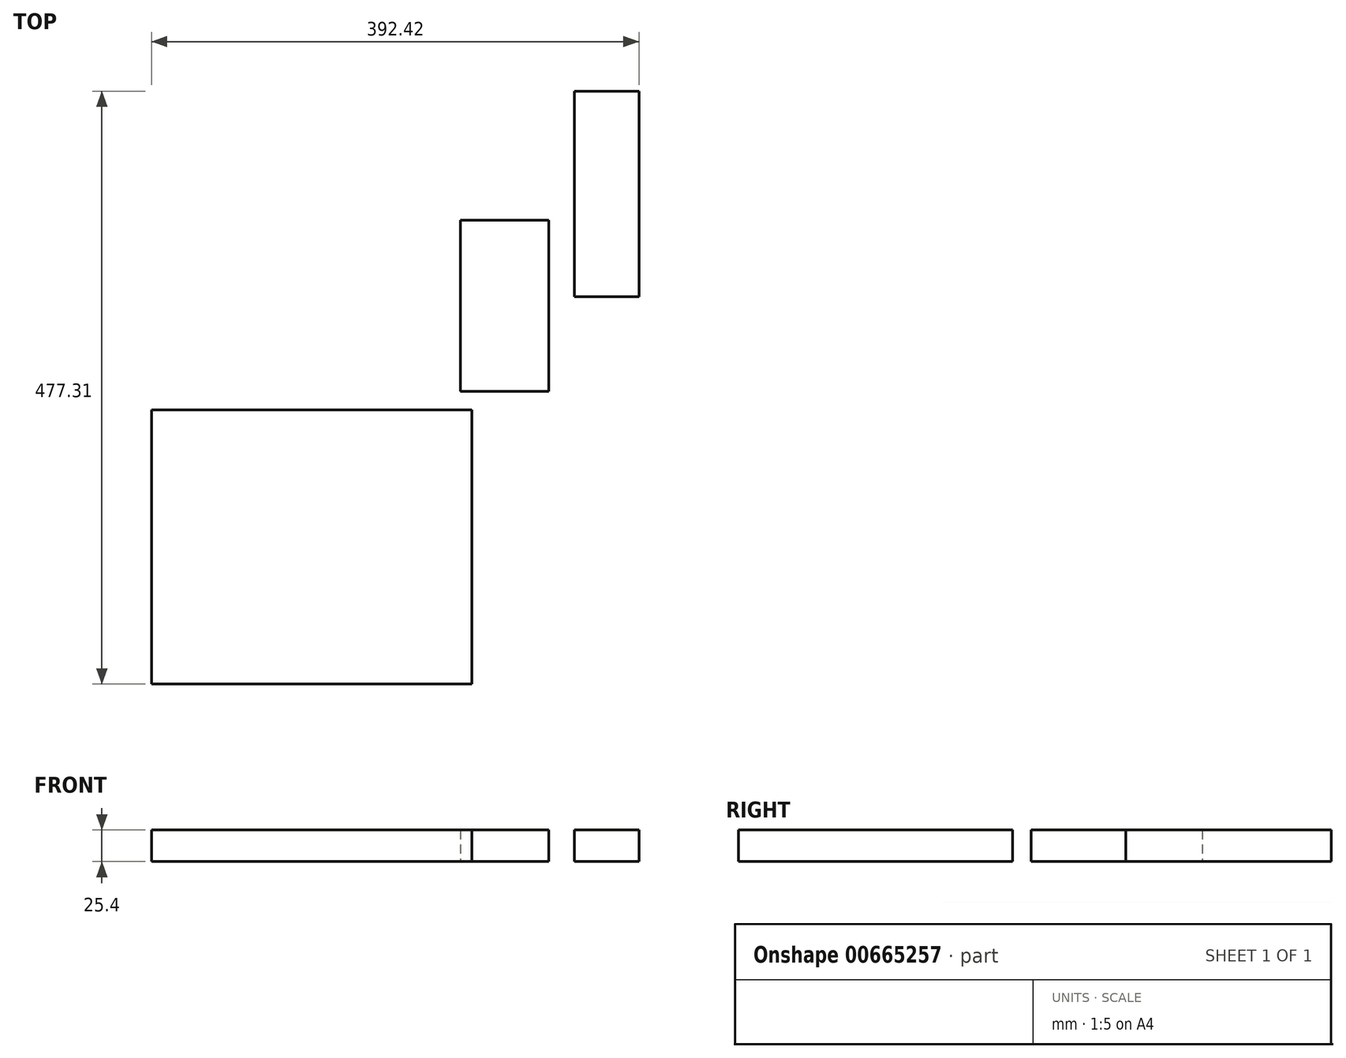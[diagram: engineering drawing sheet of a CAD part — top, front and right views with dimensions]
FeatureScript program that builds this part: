
annotation { "Feature Type Name" : "Feature", "Feature Type Description" : "" }
export const myFeature = defineFeature(function(context is Context, id is Id, definition is map)
    precondition{}
    {
        {
            var Q0;
            Q0=qCreatedBy(makeId("Top.planeOp"),FACE);
            var sketch = newSketch(context, id + "F0", { "sketchPlane" : qUnion([Q0])});
            skLineSegment(sketch, "E0.bottom", {"start": v(-319.78, -311.93) * mm, "end": v(-61.8, -311.93) * mm});
            skLineSegment(sketch, "E0.top", {"start": v(-319.78, -91.25) * mm, "end": v(-61.8, -91.25) * mm});
            skLineSegment(sketch, "E0.left", {"start": v(-319.78, -311.93) * mm, "end": v(-319.78, -91.25) * mm});
            skLineSegment(sketch, "E0.right", {"start": v(-61.8, -311.93) * mm, "end": v(-61.8, -91.25) * mm});
            skLineSegment(sketch, "E1.bottom", {"start": v(0, 61.52) * mm, "end": v(-71.1, 61.52) * mm});
            skLineSegment(sketch, "E1.top", {"start": v(0, -76.29) * mm, "end": v(-71.1, -76.29) * mm});
            skLineSegment(sketch, "E1.left", {"start": v(0, 61.52) * mm, "end": v(0, -76.29) * mm});
            skLineSegment(sketch, "E1.right", {"start": v(-71.1, 61.52) * mm, "end": v(-71.1, -76.29) * mm});
            skLineSegment(sketch, "E2.bottom", {"start": v(72.64, 165.38) * mm, "end": v(20.66, 165.38) * mm});
            skLineSegment(sketch, "E2.top", {"start": v(72.64, 0) * mm, "end": v(20.66, 0) * mm});
            skLineSegment(sketch, "E2.left", {"start": v(72.64, 165.38) * mm, "end": v(72.64, 0) * mm});
            skLineSegment(sketch, "E2.right", {"start": v(20.66, 165.38) * mm, "end": v(20.66, 0) * mm});
            skSolve(sketch);
        }
        {
            var Q0;
            Q0 = qSketchRegion(id + "F0", true);
            extrude(context, id + "F1", {"entities" : qUnion([Q0]), "depth" : 25.4 * mm, "offsetDistance" : 25.4 * mm});
        }
    });
